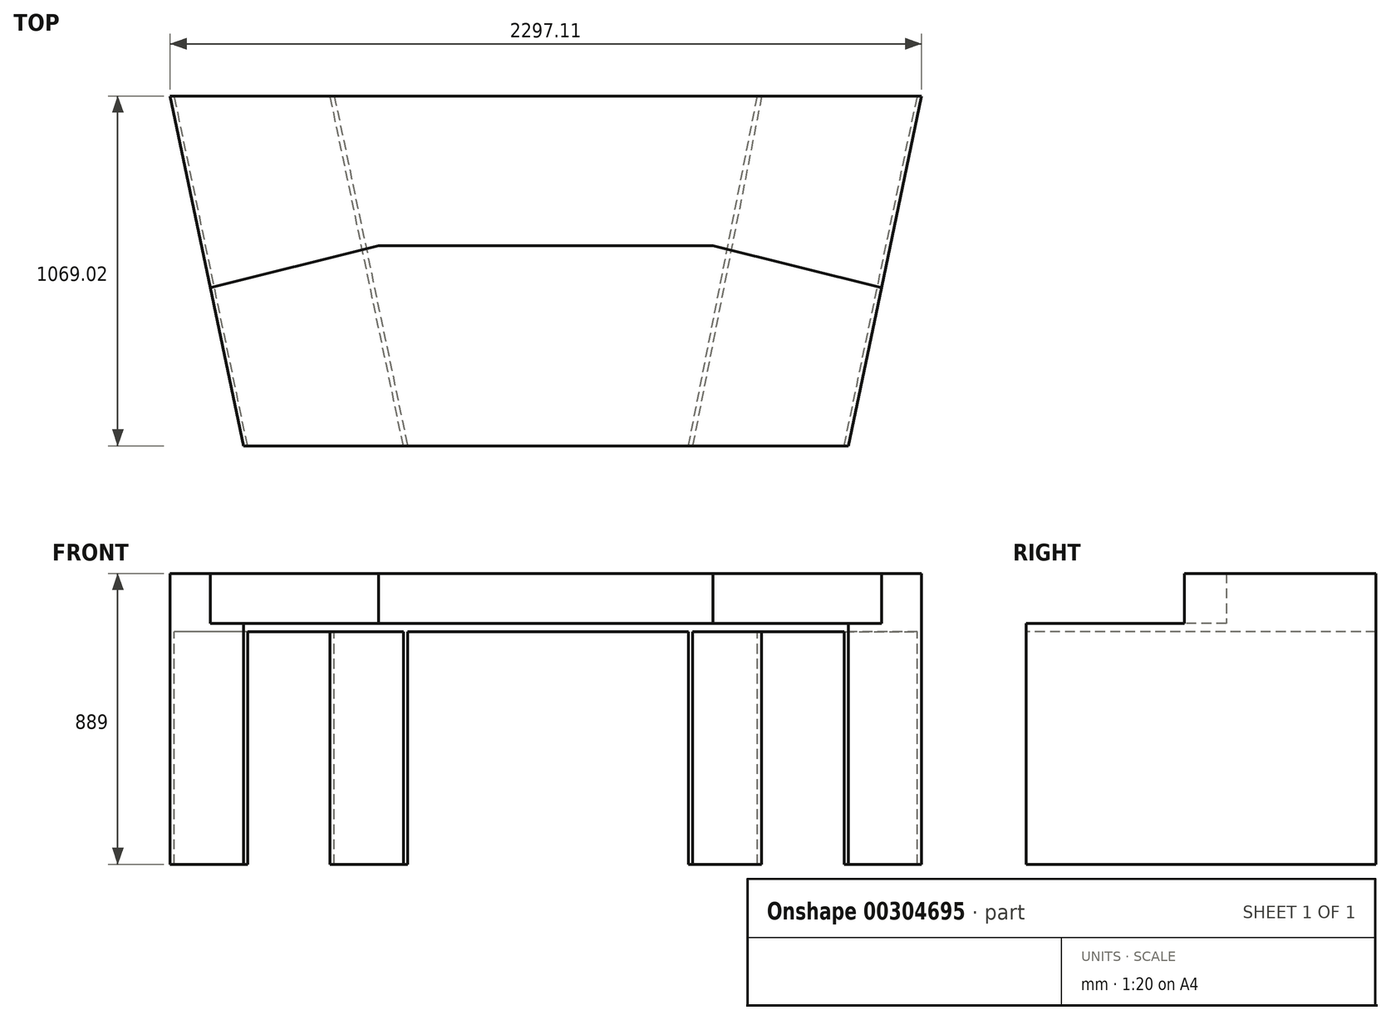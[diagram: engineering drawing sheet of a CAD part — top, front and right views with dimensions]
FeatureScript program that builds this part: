
annotation { "Feature Type Name" : "Feature", "Feature Type Description" : "" }
export const myFeature = defineFeature(function(context is Context, id is Id, definition is map)
    precondition{}
    {
        {
            var Q0;
            Q0=qCreatedBy(makeId("Top.planeOp"),FACE);
            var sketch = newSketch(context, id + "F0", { "sketchPlane" : qUnion([Q0])});
            skLineSegment(sketch, "E0", {"start": v(-599.7, -489.32) * mm, "end": v(1249.73, -489.32) * mm});
            skLineSegment(sketch, "E1", {"start": v(1249.73, -489.32) * mm, "end": v(1473.57, 579.7) * mm});
            skLineSegment(sketch, "E2", {"start": v(1473.57, 579.7) * mm, "end": v(-823.54, 579.7) * mm});
            skLineSegment(sketch, "E3", {"start": v(-823.54, 579.7) * mm, "end": v(-599.7, -489.32) * mm});
            skSolve(sketch);
        }
        {
            var Q0;
            Q0=makeQuery(id+"F0.imprint","IMPRINT",FACE,{"disambiguationData":[TD([[makeQuery(id+"F0.imprint","IMPRINT",EDGE,{"derivedFrom":sQuery(id+"F0.wireOp",EDGE,"E0")}),1.0]])]});
            extrude(context, id + "F1", {"entities" : qUnion([Q0]), "depth" : 25.4 * mm});
        }
        {
            var Q0;
            Q0=makeQuery(id+"F1.opExtrude","CAP_FACE",FACE,{"disambiguationData":[OSD([sQuery(id+"F0.wireOp",EDGE,"E0"),sQuery(id+"F0.wireOp",EDGE,"E1"),sQuery(id+"F0.wireOp",EDGE,"E2"),sQuery(id+"F0.wireOp",EDGE,"E3")])],"isStart":false});
            var sketch = newSketch(context, id + "F2", { "sketchPlane" : qUnion([Q0])});
            skLineSegment(sketch, "E4", {"start": v(-823.54, 579.7) * mm, "end": v(1473.57, 579.7) * mm});
            skLineSegment(sketch, "E5", {"start": v(1473.57, 579.7) * mm, "end": v(1350.92, -6.09) * mm});
            skLineSegment(sketch, "E6", {"start": v(-700.88, -6.09) * mm, "end": v(-823.54, 579.7) * mm});
            skLineSegment(sketch, "E7", {"start": v(-700.88, -6.09) * mm, "end": v(-186.15, 122.5) * mm});
            skLineSegment(sketch, "E8", {"start": v(-186.15, 122.5) * mm, "end": v(836.2, 122.5) * mm});
            skLineSegment(sketch, "E9", {"start": v(836.2, 122.5) * mm, "end": v(1350.92, -6.09) * mm});
            skSolve(sketch);
        }
        {
            var Q0;
            Q0=makeQuery(id+"F2.imprint","IMPRINT",FACE,{"disambiguationData":[TD([[makeQuery(id+"F2.imprint","IMPRINT",EDGE,{"derivedFrom":sQuery(id+"F2.wireOp",EDGE,"E4")}),1.0]])]});
            extrude(context, id + "F3", {"entities" : qUnion([Q0]), "operationType" : NewBodyOperationType.ADD, "depth" : 152.4 * mm});
        }
        {
            var Q0;
            Q0=makeQuery(id+"F1.opExtrude","CAP_FACE",FACE,{"disambiguationData":[OSD([sQuery(id+"F0.wireOp",EDGE,"E0"),sQuery(id+"F0.wireOp",EDGE,"E1"),sQuery(id+"F0.wireOp",EDGE,"E2"),sQuery(id+"F0.wireOp",EDGE,"E3")])],"isStart":true});
            var sketch = newSketch(context, id + "F4", { "sketchPlane" : qUnion([Q0])});
            skLineSegment(sketch, "E10", {"start": v(1249.73, 489.32) * mm, "end": v(1237.03, 489.32) * mm});
            skLineSegment(sketch, "E11", {"start": v(1237.03, 489.32) * mm, "end": v(1460.87, -579.7) * mm});
            skLineSegment(sketch, "E12", {"start": v(1460.87, -579.7) * mm, "end": v(1473.57, -579.7) * mm});
            skLineSegment(sketch, "E13", {"start": v(1473.57, -579.7) * mm, "end": v(1249.73, 489.32) * mm});
            skLineSegment(sketch, "E14", {"start": v(-823.54, -579.7) * mm, "end": v(-599.7, 489.32) * mm});
            skLineSegment(sketch, "E15", {"start": v(-599.7, 489.32) * mm, "end": v(-587, 489.32) * mm});
            skLineSegment(sketch, "E16", {"start": v(-587, 489.32) * mm, "end": v(-810.84, -579.7) * mm});
            skLineSegment(sketch, "E17", {"start": v(-810.84, -579.7) * mm, "end": v(-823.54, -579.7) * mm});
            skLineSegment(sketch, "E18", {"start": v(-110.75, 489.32) * mm, "end": v(-334.6, -579.7) * mm});
            skLineSegment(sketch, "E19", {"start": v(-334.6, -579.7) * mm, "end": v(-321.9, -579.7) * mm});
            skLineSegment(sketch, "E20", {"start": v(-321.9, -579.7) * mm, "end": v(-98.05, 489.32) * mm});
            skLineSegment(sketch, "E21", {"start": v(-98.05, 489.32) * mm, "end": v(-110.75, 489.32) * mm});
            skLineSegment(sketch, "E22", {"start": v(760.78, 489.32) * mm, "end": v(971.92, -579.7) * mm});
            skLineSegment(sketch, "E23", {"start": v(984.62, -579.7) * mm, "end": v(971.92, -579.7) * mm});
            skLineSegment(sketch, "E24", {"start": v(984.62, -579.7) * mm, "end": v(773.48, 489.32) * mm});
            skLineSegment(sketch, "E25", {"start": v(760.78, 489.32) * mm, "end": v(773.48, 489.32) * mm});
            skSolve(sketch);
        }
        {
            var Q0;
            Q0=makeQuery(id+"F4.imprint","IMPRINT",FACE,{"disambiguationData":[TD([[makeQuery(id+"F4.imprint","IMPRINT",EDGE,{"derivedFrom":sQuery(id+"F4.wireOp",EDGE,"E14")}),-1.0]])]});
            var Q1;
            Q1=makeQuery(id+"F4.imprint","IMPRINT",FACE,{"disambiguationData":[TD([[makeQuery(id+"F4.imprint","IMPRINT",EDGE,{"derivedFrom":sQuery(id+"F4.wireOp",EDGE,"E18")}),1.0]])]});
            var Q2;
            Q2=makeQuery(id+"F4.imprint","IMPRINT",FACE,{"disambiguationData":[TD([[makeQuery(id+"F4.imprint","IMPRINT",EDGE,{"derivedFrom":sQuery(id+"F4.wireOp",EDGE,"E22")}),1.0]])]});
            var Q3;
            Q3=makeQuery(id+"F4.imprint","IMPRINT",FACE,{"disambiguationData":[TD([[makeQuery(id+"F4.imprint","IMPRINT",EDGE,{"derivedFrom":sQuery(id+"F4.wireOp",EDGE,"E10")}),-1.0]])]});
            extrude(context, id + "F5", {"entities" : qUnion([Q0, Q1, Q2, Q3]), "operationType" : NewBodyOperationType.ADD, "depth" : 711.2 * mm});
        }
    });
